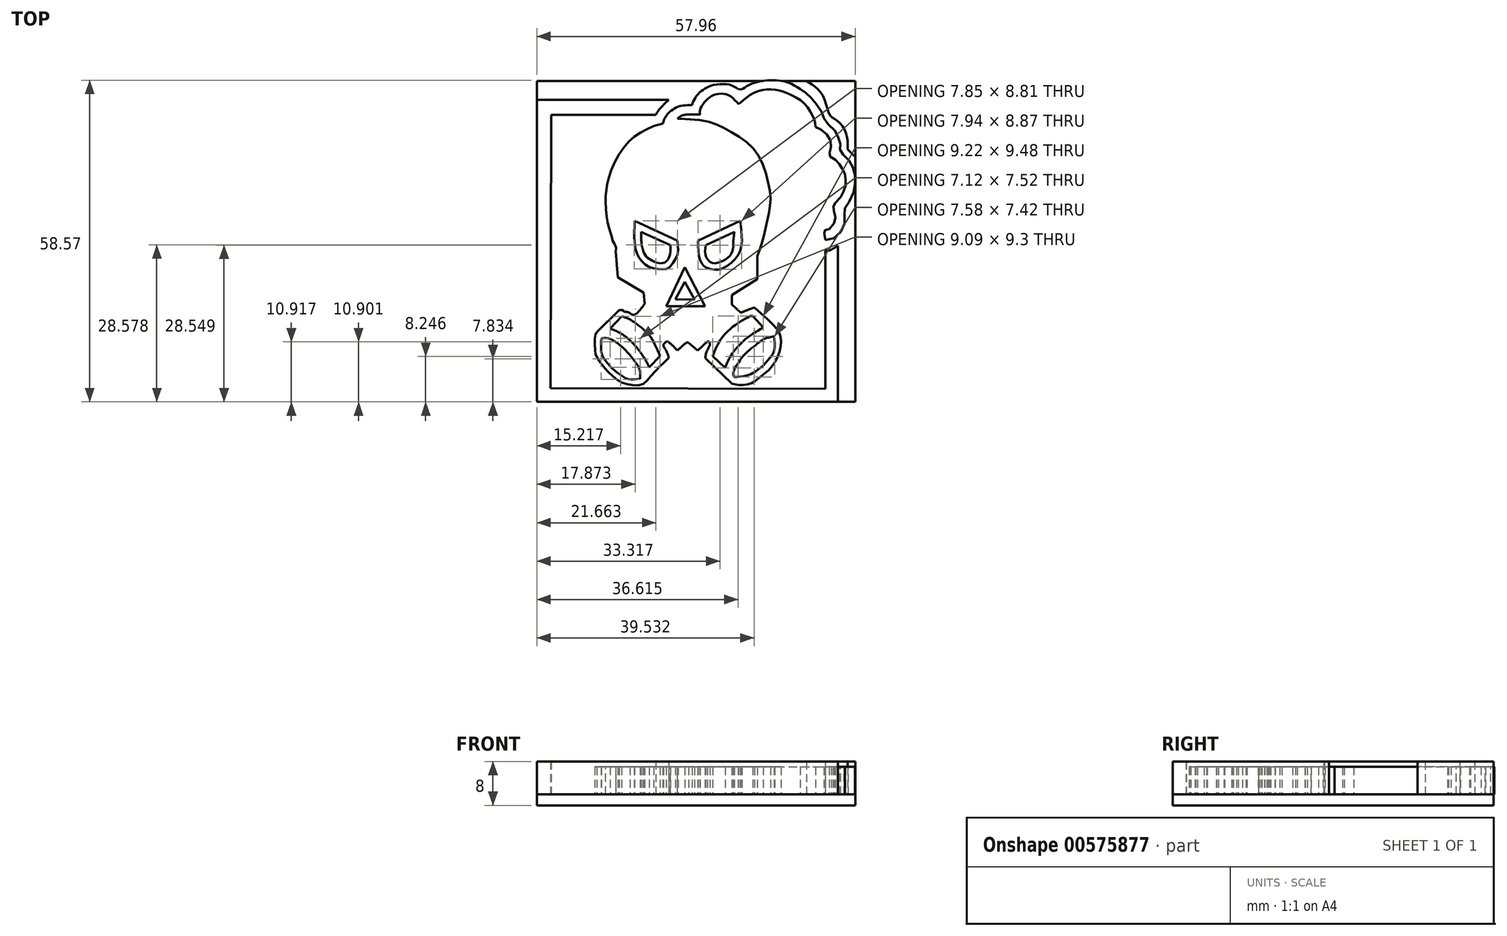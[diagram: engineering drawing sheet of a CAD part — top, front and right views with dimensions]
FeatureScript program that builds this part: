
annotation { "Feature Type Name" : "Feature", "Feature Type Description" : "" }
export const myFeature = defineFeature(function(context is Context, id is Id, definition is map)
    precondition{}
    {
        {
            var Q0;
            Q0=qCreatedBy(makeId("Top.planeOp"),FACE);
            var sketch = newSketch(context, id + "F0", { "sketchPlane" : qUnion([Q0])});
            skFitSpline(sketch, "E0", {"points": [v(4.85, 4.86) * mm, v(54.85, 4.78) * mm], "startDerivative": vector(50, -0.08) * mm, "endDerivative": vector(50, -0.08) * mm});
            skFitSpline(sketch, "E1", {"points": [v(54.85, 4.78) * mm, v(54.85, 29.74) * mm], "startDerivative": vector(0, 24.96) * mm, "endDerivative": vector(0, 24.96) * mm});
            skFitSpline(sketch, "E2", {"points": [v(54.85, 29.74) * mm, v(54.85, 29.98) * mm], "startDerivative": vector(0, 0.24) * mm, "endDerivative": vector(0, 0.24) * mm});
            skFitSpline(sketch, "E3", {"points": [v(54.85, 29.98) * mm, v(55.67, 29.98) * mm, v(56.18, 30.25) * mm, v(56.7, 30.54) * mm, v(57.15, 30.84) * mm, v(57.33, 30.87) * mm], "startDerivative": vector(3.51, -0.37) * mm, "endDerivative": vector(1.39, 0) * mm});
            skFitSpline(sketch, "E4", {"points": [v(57.15, 30.84) * mm, v(57.15, 2.42) * mm], "startDerivative": vector(0, -28.42) * mm, "endDerivative": vector(0, -28.42) * mm});
            skFitSpline(sketch, "E5", {"points": [v(57.15, 2.42) * mm, v(2.35, 2.42) * mm], "startDerivative": vector(-54.8, 0) * mm, "endDerivative": vector(-54.8, 0) * mm});
            skFitSpline(sketch, "E6", {"points": [v(2.35, 2.42) * mm, v(2.35, 57.4) * mm], "startDerivative": vector(0, 54.94) * mm, "endDerivative": vector(0, 54.94) * mm});
            skFitSpline(sketch, "E7", {"points": [v(2.35, 57.4) * mm, v(26.35, 57.4) * mm], "startDerivative": vector(24.68, 0) * mm, "endDerivative": vector(24.68, 0) * mm});
            skFitSpline(sketch, "E8", {"points": [v(26.35, 57.4) * mm, v(23.98, 54.66) * mm, v(23.63, 52.6) * mm], "startDerivative": vector(-5.14, -4.83) * mm, "endDerivative": vector(-0.06, -4.77) * mm});
            skFitSpline(sketch, "E9", {"points": [v(23.63, 52.6) * mm, v(25.28, 53.05) * mm], "startDerivative": vector(1.65, 0.45) * mm, "endDerivative": vector(1.65, 0.45) * mm});
            skFitSpline(sketch, "E10", {"points": [v(25.28, 53.05) * mm, v(25.4, 53.54) * mm, v(25.65, 54.08) * mm, v(25.98, 54.6) * mm, v(26.48, 55.15) * mm, v(27.56, 55.93) * mm, v(28.84, 56.34) * mm, v(30.58, 56.44) * mm], "startDerivative": vector(0.94, 4.7) * mm, "endDerivative": vector(9.33, 0.14) * mm});
            skFitSpline(sketch, "E11", {"points": [v(30.58, 56.44) * mm, v(30.96, 57.4) * mm, v(31.85, 58.59) * mm, v(32.94, 59.45) * mm, v(34.64, 60.13) * mm, v(37.51, 60.13) * mm, v(38.97, 59.36) * mm], "startDerivative": vector(2.28, 7.29) * mm, "endDerivative": vector(8.97, -6.09) * mm});
            skFitSpline(sketch, "E12", {"points": [v(38.97, 59.36) * mm, v(40.18, 59.65) * mm, v(41.42, 60.33) * mm, v(43.29, 60.8) * mm, v(45.6, 60.95) * mm, v(47.88, 60.62) * mm, v(50.28, 59.36) * mm], "startDerivative": vector(14.4, -4.18) * mm, "endDerivative": vector(11.74, -8.26) * mm});
            skFitSpline(sketch, "E13", {"points": [v(50.28, 59.36) * mm, v(51.28, 58.67) * mm, v(52.3, 57.74) * mm, v(53.42, 56.38) * mm, v(54.43, 54.7) * mm, v(54.73, 53.63) * mm, v(56.28, 52.13) * mm, v(56.93, 51.29) * mm, v(57.5, 49.79) * mm, v(57.63, 48.77) * mm, v(57.55, 48) * mm, v(58.55, 47.04) * mm, v(59.65, 45.6) * mm, v(60.17, 44.12) * mm, v(60.27, 42.4) * mm, v(59.9, 40.3) * mm, v(58.72, 38.04) * mm, v(58.3, 37.37) * mm, v(58.43, 35.77) * mm, v(57.88, 33.68) * mm, v(56.25, 32.12) * mm, v(54.38, 31.93) * mm, v(52.6, 32) * mm, v(52, 30.53) * mm, v(56.18, 30.25) * mm], "startDerivative": vector(28.59, -18.45) * mm, "endDerivative": vector(86.4, 9.51) * mm});
            skFitSpline(sketch, "E14", {"points": [v(58.93, 48.37) * mm, v(60.3, 46.96) * mm], "startDerivative": vector(1.38, -1.41) * mm, "endDerivative": vector(1.38, -1.41) * mm});
            skFitSpline(sketch, "E15", {"points": [v(60.3, 46.96) * mm, v(60.3, 60.84) * mm], "startDerivative": vector(0, 13.88) * mm, "endDerivative": vector(0, 13.88) * mm});
            skFitSpline(sketch, "E16", {"points": [v(60.3, 60.84) * mm, v(51.45, 60.84) * mm], "startDerivative": vector(-8.86, 0) * mm, "endDerivative": vector(-8.86, 0) * mm});
            skFitSpline(sketch, "E17", {"points": [v(51.45, 60.84) * mm, v(53, 59.77) * mm, v(54.72, 57.45) * mm, v(55.67, 54.6) * mm, v(56.8, 53.72) * mm, v(58.28, 52.11) * mm, v(58.93, 49.68) * mm, v(58.93, 48.37) * mm], "startDerivative": vector(11.4, -6.9) * mm, "endDerivative": vector(-0.57, -10.61) * mm});
            skFitSpline(sketch, "E18", {"points": [v(16.54, 29.62) * mm, v(16.7, 29.74) * mm], "startDerivative": vector(0.15, 0.12) * mm, "endDerivative": vector(0.15, 0.12) * mm});
            skFitSpline(sketch, "E19", {"points": [v(16.7, 29.74) * mm, v(17.07, 25.04) * mm], "startDerivative": vector(0.37, -4.7) * mm, "endDerivative": vector(0.37, -4.7) * mm});
            skFitSpline(sketch, "E20", {"points": [v(17.07, 25.04) * mm, v(21.8, 22.26) * mm], "startDerivative": vector(4.74, -2.78) * mm, "endDerivative": vector(4.74, -2.78) * mm});
            skFitSpline(sketch, "E21", {"points": [v(21.8, 22.26) * mm, v(21.95, 20.22) * mm], "startDerivative": vector(0.14, -2.03) * mm, "endDerivative": vector(0.14, -2.03) * mm});
            skFitSpline(sketch, "E22", {"points": [v(21.95, 20.22) * mm, v(20.25, 18.31) * mm, v(19.67, 18.28) * mm, v(19.28, 18.51) * mm], "startDerivative": vector(-3.51, -4.76) * mm, "endDerivative": vector(-1.67, 1.18) * mm});
            skFitSpline(sketch, "E23", {"points": [v(19.28, 18.51) * mm, v(18.83, 18.74) * mm, v(18.1, 18.88) * mm, v(18.06, 19.06) * mm, v(17.34, 19.1) * mm], "startDerivative": vector(-1.44, 1.12) * mm, "endDerivative": vector(-3.3, -0.3) * mm});
            skFitSpline(sketch, "E24", {"points": [v(17.34, 19.1) * mm, v(13.24, 15.08) * mm], "startDerivative": vector(-4.1, -4.02) * mm, "endDerivative": vector(-4.1, -4.02) * mm});
            skFitSpline(sketch, "E25", {"points": [v(13.24, 15.08) * mm, v(13, 14.65) * mm, v(12.9, 13.24) * mm, v(12.98, 11.35) * mm, v(13.24, 10.59) * mm, v(13.87, 9.58) * mm, v(14.67, 8.6) * mm, v(15.98, 7.23) * mm, v(17.7, 5.97) * mm, v(19.28, 5.5) * mm, v(21.4, 5.49) * mm, v(22.73, 6.67) * mm, v(24.54, 8.6) * mm, v(26.35, 10.39) * mm], "startDerivative": vector(-6.78, -8.44) * mm, "endDerivative": vector(18.54, 18.04) * mm});
            skFitSpline(sketch, "E26", {"points": [v(26.35, 10.39) * mm, v(26.2, 10.94) * mm, v(25.84, 11.8) * mm, v(25.4, 12.73) * mm, v(25.92, 13.33) * mm], "startDerivative": vector(-0.59, 2.55) * mm, "endDerivative": vector(3.08, 2.22) * mm});
            skFitSpline(sketch, "E27", {"points": [v(25.92, 13.33) * mm, v(26.18, 13.33) * mm, v(27.85, 11.83) * mm], "startDerivative": vector(0.88, 0.26) * mm, "endDerivative": vector(2.68, -2.76) * mm});
            skFitSpline(sketch, "E28", {"points": [v(27.85, 11.83) * mm, v(27.96, 11.75) * mm], "startDerivative": vector(0.12, -0.08) * mm, "endDerivative": vector(0.12, -0.08) * mm});
            skFitSpline(sketch, "E29", {"points": [v(27.96, 11.75) * mm, v(29.62, 13.15) * mm, v(29.98, 13.14) * mm], "startDerivative": vector(2.72, 2.7) * mm, "endDerivative": vector(1.08, -0.33) * mm});
            skFitSpline(sketch, "E30", {"points": [v(29.98, 13.14) * mm, v(31.63, 11.75) * mm], "startDerivative": vector(1.65, -1.4) * mm, "endDerivative": vector(1.65, -1.4) * mm});
            skFitSpline(sketch, "E31", {"points": [v(31.63, 11.75) * mm, v(33.39, 13.41) * mm], "startDerivative": vector(1.76, 1.66) * mm, "endDerivative": vector(1.76, 1.66) * mm});
            skFitSpline(sketch, "E32", {"points": [v(33.39, 13.41) * mm, v(33.78, 13.17) * mm, v(33.79, 12.62) * mm, v(33.5, 12) * mm, v(33.1, 11.04) * mm, v(33.04, 10.3) * mm], "startDerivative": vector(2.94, -1.02) * mm, "endDerivative": vector(0.03, -3.37) * mm});
            skFitSpline(sketch, "E33", {"points": [v(33.04, 10.3) * mm, v(37.84, 5.7) * mm], "startDerivative": vector(4.8, -4.6) * mm, "endDerivative": vector(4.8, -4.6) * mm});
            skFitSpline(sketch, "E34", {"points": [v(37.84, 5.7) * mm, v(39.15, 5.47) * mm, v(41.21, 5.7) * mm, v(42.6, 6.64) * mm, v(44.47, 8.08) * mm, v(46.27, 10.75) * mm, v(46.79, 13.41) * mm, v(46.36, 15.17) * mm, v(41.94, 19.55) * mm], "startDerivative": vector(13.23, -3.15) * mm, "endDerivative": vector(-28.34, 24.51) * mm});
            skFitSpline(sketch, "E35", {"points": [v(41.94, 19.55) * mm, v(41.4, 19.38) * mm, v(40.3, 18.96) * mm, v(39.46, 18.63) * mm], "startDerivative": vector(-1.82, -0.5) * mm, "endDerivative": vector(-2.31, -0.92) * mm});
            skFitSpline(sketch, "E36", {"points": [v(39.46, 18.63) * mm, v(37.84, 20.08) * mm], "startDerivative": vector(-1.62, 1.46) * mm, "endDerivative": vector(-1.62, 1.46) * mm});
            skFitSpline(sketch, "E37", {"points": [v(37.84, 20.08) * mm, v(37.84, 21.85) * mm], "startDerivative": vector(0, 1.77) * mm, "endDerivative": vector(0, 1.77) * mm});
            skFitSpline(sketch, "E38", {"points": [v(37.84, 21.85) * mm, v(42.47, 24.74) * mm], "startDerivative": vector(4.64, 2.9) * mm, "endDerivative": vector(4.64, 2.9) * mm});
            skFitSpline(sketch, "E39", {"points": [v(42.47, 24.74) * mm, v(42.47, 28.94) * mm], "startDerivative": vector(0, 4.2) * mm, "endDerivative": vector(0, 4.2) * mm});
            skFitSpline(sketch, "E40", {"points": [v(42.47, 28.94) * mm, v(43.34, 31.38) * mm, v(44.23, 35.3) * mm, v(44.87, 38.88) * mm, v(44.27, 43.1) * mm, v(41.94, 48.3) * mm, v(37.84, 51.46) * mm, v(33.85, 53.32) * mm, v(27.96, 53.99) * mm], "startDerivative": vector(9.51, 23.54) * mm, "endDerivative": vector(-43.14, 2.06) * mm});
            skFitSpline(sketch, "E41", {"points": [v(27.96, 53.99) * mm, v(28.4, 53.97) * mm], "startDerivative": vector(0.45, -0.02) * mm, "endDerivative": vector(0.45, -0.02) * mm});
            skFitSpline(sketch, "E42", {"points": [v(27.96, 53.99) * mm, v(29.02, 54.6) * mm, v(32.05, 54.69) * mm], "startDerivative": vector(2.29, 1.89) * mm, "endDerivative": vector(5.64, -0.33) * mm});
            skFitSpline(sketch, "E43", {"points": [v(32.05, 54.69) * mm, v(32.05, 55.57) * mm, v(33.04, 57.17) * mm, v(34.77, 58.34) * mm, v(37.17, 58.3) * mm, v(39.02, 56.6) * mm], "startDerivative": vector(-0.96, 6.05) * mm, "endDerivative": vector(7.21, -8.91) * mm});
            skFitSpline(sketch, "E44", {"points": [v(39.02, 56.6) * mm, v(40.03, 57.4) * mm, v(41.5, 58.49) * mm, v(43.51, 59.2) * mm, v(45.5, 59.28) * mm, v(47.22, 58.85) * mm, v(49.66, 57.75) * mm, v(51.6, 56.06) * mm, v(52.9, 53.61) * mm, v(53.07, 52.43) * mm], "startDerivative": vector(10.88, 8.42) * mm, "endDerivative": vector(0.5, -12.4) * mm});
            skFitSpline(sketch, "E45", {"points": [v(53.07, 52.43) * mm, v(54.07, 51.95) * mm, v(55.44, 50.7) * mm, v(55.92, 49.33) * mm, v(55.69, 47.96) * mm, v(55.57, 47.48) * mm, v(55.87, 46.94) * mm, v(56.88, 46.35) * mm, v(57.48, 45.57) * mm, v(57.95, 44.8) * mm, v(58.43, 43.78) * mm, v(58.55, 42.7) * mm, v(58.5, 41.46) * mm, v(58.02, 40.33) * mm, v(57.31, 39.2) * mm, v(56.24, 38.13) * mm, v(56.42, 37.71) * mm, v(56.48, 36.52) * mm, v(56.72, 35.69) * mm, v(56.07, 34.38) * mm, v(55.12, 33.6) * mm, v(54.65, 33.61) * mm, v(54.68, 33.21) * mm, v(54.84, 31.87) * mm], "startDerivative": vector(20.86, -8.3) * mm, "endDerivative": vector(7.9, -24.33) * mm});
            skFitSpline(sketch, "E46", {"points": [v(18.23, 25.9) * mm, v(22.93, 22.86) * mm], "startDerivative": vector(4.7, -3.05) * mm, "endDerivative": vector(4.7, -3.05) * mm});
            skFitSpline(sketch, "E47", {"points": [v(22.93, 22.86) * mm, v(22.93, 19.55) * mm], "startDerivative": vector(0, -3.3) * mm, "endDerivative": vector(0, -3.3) * mm});
            skFitSpline(sketch, "E48", {"points": [v(22.93, 19.55) * mm, v(21.19, 17.92) * mm], "startDerivative": vector(-1.74, -1.64) * mm, "endDerivative": vector(-1.74, -1.64) * mm});
            skFitSpline(sketch, "E49", {"points": [v(21.19, 17.92) * mm, v(22.5, 17.06) * mm, v(23.49, 16.03) * mm, v(24.4, 14.83) * mm, v(24.82, 14.03) * mm, v(25.12, 13.96) * mm, v(25.53, 14.45) * mm, v(25.97, 14.79) * mm, v(26.34, 14.8) * mm, v(26.78, 14.27) * mm, v(27.2, 13.9) * mm, v(27.93, 13.19) * mm], "startDerivative": vector(10.98, -6.4) * mm, "endDerivative": vector(7.58, -7.87) * mm});
            skFitSpline(sketch, "E50", {"points": [v(27.93, 13.19) * mm, v(29.79, 14.92) * mm], "startDerivative": vector(1.85, 1.73) * mm, "endDerivative": vector(1.85, 1.73) * mm});
            skFitSpline(sketch, "E51", {"points": [v(29.79, 14.92) * mm, v(31.6, 13.19) * mm], "startDerivative": vector(1.82, -1.73) * mm, "endDerivative": vector(1.82, -1.73) * mm});
            skFitSpline(sketch, "E52", {"points": [v(31.6, 13.19) * mm, v(33.44, 14.92) * mm], "startDerivative": vector(1.83, 1.73) * mm, "endDerivative": vector(1.83, 1.73) * mm});
            skFitSpline(sketch, "E53", {"points": [v(33.44, 14.92) * mm, v(34.61, 13.96) * mm], "startDerivative": vector(1.17, -0.95) * mm, "endDerivative": vector(1.17, -0.95) * mm});
            skFitSpline(sketch, "E54", {"points": [v(34.61, 13.96) * mm, v(34.61, 14.41) * mm, v(35.43, 15.54) * mm, v(36.28, 16.46) * mm, v(38.2, 17.92) * mm], "startDerivative": vector(-0.63, 2.75) * mm, "endDerivative": vector(6.33, 4.47) * mm});
            skFitSpline(sketch, "E55", {"points": [v(38.2, 17.92) * mm, v(36.53, 19.55) * mm], "startDerivative": vector(-1.68, 1.64) * mm, "endDerivative": vector(-1.68, 1.64) * mm});
            skFitSpline(sketch, "E56", {"points": [v(36.53, 19.55) * mm, v(36.53, 22.86) * mm], "startDerivative": vector(0, 3.3) * mm, "endDerivative": vector(0, 3.3) * mm});
            skFitSpline(sketch, "E57", {"points": [v(36.53, 22.86) * mm, v(41.34, 25.9) * mm], "startDerivative": vector(4.81, 3.05) * mm, "endDerivative": vector(4.81, 3.05) * mm});
            skFitSpline(sketch, "E58", {"points": [v(41.34, 25.9) * mm, v(41.34, 29.15) * mm, v(42, 31.3) * mm, v(42.47, 33.75) * mm, v(43.2, 36.6) * mm, v(43.18, 41.86) * mm, v(41.34, 46.73) * mm, v(37.85, 50.02) * mm, v(35.13, 51.62) * mm], "startDerivative": vector(-2.15, 28.98) * mm, "endDerivative": vector(-23.66, 9.66) * mm});
            skFitSpline(sketch, "E59", {"points": [v(35.13, 51.62) * mm, v(34.47, 51.85) * mm, v(32.8, 52.45) * mm, v(31.13, 52.77) * mm, v(29.24, 52.9) * mm, v(27.39, 52.57) * mm, v(25.25, 51.88) * mm, v(23.7, 51.34) * mm, v(21.93, 50.33) * mm, v(20.35, 49.26) * mm, v(18.93, 47.6) * mm, v(18.13, 46.15) * mm, v(17.28, 44.31) * mm, v(16.51, 41.94) * mm, v(16.21, 40.6) * mm, v(16.22, 36.88) * mm, v(16.7, 35.08) * mm, v(17.17, 33.36) * mm, v(17.64, 31.54) * mm, v(17.9, 29.94) * mm, v(18.15, 26.66) * mm, v(18.23, 25.9) * mm], "startDerivative": vector(-19.6, 6.77) * mm, "endDerivative": vector(2.06, -18.95) * mm});
            skFitSpline(sketch, "E60", {"points": [v(27.58, 21.04) * mm, v(29.3, 24.23) * mm], "startDerivative": vector(1.7, 3.18) * mm, "endDerivative": vector(1.7, 3.18) * mm});
            skFitSpline(sketch, "E61", {"points": [v(29.3, 24.23) * mm, v(31.07, 20.98) * mm], "startDerivative": vector(1.77, -3.24) * mm, "endDerivative": vector(1.77, -3.24) * mm});
            skFitSpline(sketch, "E62", {"points": [v(31.07, 20.98) * mm, v(27.58, 21.04) * mm], "startDerivative": vector(-3.48, 0.06) * mm, "endDerivative": vector(-3.48, 0.06) * mm});
            skFitSpline(sketch, "E63", {"points": [v(25.88, 19.8) * mm, v(32.94, 19.82) * mm], "startDerivative": vector(7.06, 0.02) * mm, "endDerivative": vector(7.06, 0.02) * mm});
            skFitSpline(sketch, "E64", {"points": [v(32.94, 19.82) * mm, v(29.3, 26.88) * mm], "startDerivative": vector(-3.65, 7.05) * mm, "endDerivative": vector(-3.65, 7.05) * mm});
            skFitSpline(sketch, "E65", {"points": [v(29.3, 26.88) * mm, v(25.88, 19.8) * mm], "startDerivative": vector(-3.41, -7.07) * mm, "endDerivative": vector(-3.41, -7.07) * mm});
            skFitSpline(sketch, "E66", {"points": [v(26.64, 30.89) * mm, v(21.31, 33.31) * mm], "startDerivative": vector(-5.33, 2.43) * mm, "endDerivative": vector(-5.33, 2.43) * mm});
            skFitSpline(sketch, "E67", {"points": [v(33.07, 30.89) * mm, v(33.07, 29.07) * mm, v(34.17, 27.7) * mm, v(35.97, 27.95) * mm, v(37.23, 28.75) * mm, v(37.99, 29.92) * mm, v(38.11, 31.29) * mm, v(38.28, 33.31) * mm], "startDerivative": vector(-1.6, -12.2) * mm, "endDerivative": vector(1.39, 13.4) * mm});
            skFitSpline(sketch, "E68", {"points": [v(38.28, 33.31) * mm, v(33.07, 30.89) * mm], "startDerivative": vector(-5.2, -2.43) * mm, "endDerivative": vector(-5.2, -2.43) * mm});
            skFitSpline(sketch, "E69", {"points": [v(27.91, 31.73) * mm, v(27.88, 29.07) * mm, v(26.64, 27.06) * mm, v(26.03, 26.64) * mm, v(23.88, 26.65) * mm, v(21.7, 27.7) * mm, v(20.4, 29.92) * mm, v(20.1, 32) * mm, v(20.13, 35.38) * mm], "startDerivative": vector(2.63, -19.72) * mm, "endDerivative": vector(0.59, 23.4) * mm});
            skFitSpline(sketch, "E70", {"points": [v(20.13, 35.38) * mm, v(27.91, 31.73) * mm], "startDerivative": vector(7.79, -3.64) * mm, "endDerivative": vector(7.79, -3.64) * mm});
            skFitSpline(sketch, "E71", {"points": [v(39.39, 35.38) * mm, v(39.64, 32.59) * mm, v(39.35, 29.92) * mm, v(37.76, 27.7) * mm, v(35.97, 26.61) * mm, v(35.28, 26.5) * mm, v(33.4, 26.7) * mm, v(32.3, 27.7) * mm, v(31.83, 29.07) * mm, v(31.7, 31.73) * mm], "startDerivative": vector(2.48, -21) * mm, "endDerivative": vector(-0.18, 22.42) * mm});
            skFitSpline(sketch, "E72", {"points": [v(31.7, 31.73) * mm, v(39.39, 35.38) * mm], "startDerivative": vector(7.69, 3.64) * mm, "endDerivative": vector(7.69, 3.64) * mm});
            skFitSpline(sketch, "E73", {"points": [v(15.68, 15.73) * mm, v(17.77, 17.96) * mm], "startDerivative": vector(2.1, 2.23) * mm, "endDerivative": vector(2.1, 2.23) * mm});
            skFitSpline(sketch, "E74", {"points": [v(17.77, 17.96) * mm, v(18.64, 17.68) * mm, v(19.86, 17.03) * mm, v(21.02, 16.18) * mm, v(22.45, 14.96) * mm, v(23.63, 13.2) * mm, v(24.77, 10.72) * mm], "startDerivative": vector(6.78, -1.82) * mm, "endDerivative": vector(5.28, -12.24) * mm});
            skFitSpline(sketch, "E75", {"points": [v(24.77, 10.72) * mm, v(22.8, 8.66) * mm], "startDerivative": vector(-1.97, -2.06) * mm, "endDerivative": vector(-1.97, -2.06) * mm});
            skFitSpline(sketch, "E76", {"points": [v(22.8, 8.66) * mm, v(22.3, 9.7) * mm, v(20.39, 12.45) * mm], "startDerivative": vector(-0.9, 2.26) * mm, "endDerivative": vector(-2.04, 2.2) * mm});
            skFitSpline(sketch, "E77", {"points": [v(20.39, 12.45) * mm, v(19.43, 13.45) * mm, v(18.3, 14.4) * mm, v(16.93, 15.2) * mm, v(15.68, 15.73) * mm], "startDerivative": vector(-3.83, 4.12) * mm, "endDerivative": vector(-5.14, 1.99) * mm});
            skFitSpline(sketch, "E78", {"points": [v(34.36, 10.72) * mm, v(36.6, 8.55) * mm], "startDerivative": vector(2.25, -2.16) * mm, "endDerivative": vector(2.25, -2.16) * mm});
            skFitSpline(sketch, "E79", {"points": [v(36.6, 8.55) * mm, v(37.1, 9.75) * mm, v(37.87, 11.07) * mm, v(40.15, 13.66) * mm, v(43.57, 15.94) * mm], "startDerivative": vector(2.5, 6.71) * mm, "endDerivative": vector(11.06, 6.4) * mm});
            skFitSpline(sketch, "E80", {"points": [v(43.57, 15.94) * mm, v(41.65, 18.03) * mm], "startDerivative": vector(-1.92, 2.09) * mm, "endDerivative": vector(-1.92, 2.09) * mm});
            skFitSpline(sketch, "E81", {"points": [v(41.65, 18.03) * mm, v(41.27, 18.03) * mm, v(40.25, 17.48) * mm, v(38.13, 16.16) * mm, v(36.18, 14.24) * mm, v(35.09, 12.45) * mm, v(34.36, 10.72) * mm], "startDerivative": vector(-4.37, 0.68) * mm, "endDerivative": vector(-3.85, -9.85) * mm});
            skFitSpline(sketch, "E82", {"points": [v(45.51, 14.35) * mm, v(45.58, 11.85) * mm, v(44.47, 10.03) * mm, v(43.02, 8.55) * mm, v(42.06, 7.88) * mm, v(41.4, 7.51) * mm, v(40.3, 7.12) * mm, v(38.24, 6.92) * mm], "startDerivative": vector(2.16, -14.74) * mm, "endDerivative": vector(-12.38, 0) * mm});
            skFitSpline(sketch, "E83", {"points": [v(38.24, 6.92) * mm, v(38.24, 8.08) * mm], "startDerivative": vector(-0.6, 1.01) * mm, "endDerivative": vector(0.62, 1.06) * mm});
            skFitSpline(sketch, "E84", {"points": [v(38.24, 8.08) * mm, v(38.43, 8.54) * mm, v(39.19, 9.7) * mm, v(39.6, 10.35) * mm, v(40.83, 11.68) * mm, v(42.15, 12.7) * mm, v(43.74, 13.88) * mm, v(45.51, 14.35) * mm], "startDerivative": vector(1.35, 4.6) * mm, "endDerivative": vector(11, 4.12) * mm});
            skFitSpline(sketch, "E85", {"points": [v(21.12, 6.6) * mm, v(18.94, 6.53) * mm, v(17.65, 7.24) * mm, v(16.24, 8.3) * mm, v(14.97, 9.7) * mm, v(14.1, 11.37) * mm, v(14.12, 13.98) * mm], "startDerivative": vector(-13.43, -1.84) * mm, "endDerivative": vector(1.48, 14.42) * mm});
            skFitSpline(sketch, "E86", {"points": [v(14.12, 13.98) * mm, v(15.34, 13.98) * mm, v(16.5, 13.41) * mm, v(17.88, 12.36) * mm, v(19.43, 10.72) * mm, v(20.86, 8.7) * mm, v(21.12, 7.84) * mm, v(21.12, 6.6) * mm], "startDerivative": vector(9.8, 1) * mm, "endDerivative": vector(-0.38, -10.36) * mm});
            skFitSpline(sketch, "E87", {"points": [v(23.98, 54.66) * mm, v(4.92, 54.66) * mm], "startDerivative": vector(-19.06, 0) * mm, "endDerivative": vector(-19.06, 0) * mm});
            skFitSpline(sketch, "E88", {"points": [v(4.92, 54.66) * mm, v(4.85, 4.86) * mm], "startDerivative": vector(-0.07, -49.8) * mm, "endDerivative": vector(-0.07, -49.8) * mm});
            skFitSpline(sketch, "E89", {"points": [v(16.7, 29.74) * mm, v(16.7, 30.67) * mm, v(16.21, 31.55) * mm, v(15.96, 32.46) * mm, v(15.56, 33.82) * mm, v(15.09, 35.79) * mm, v(14.86, 39.14) * mm, v(14.98, 41) * mm, v(15.7, 44.07) * mm, v(17.9, 48.36) * mm, v(20.56, 51.04) * mm, v(23.63, 52.6) * mm], "startDerivative": vector(2.36, 16.27) * mm, "endDerivative": vector(28.37, 12.21) * mm});
            skFitSpline(sketch, "E90", {"points": [v(26.64, 30.89) * mm, v(26.64, 29.4) * mm, v(26.44, 28.82) * mm, v(26.17, 28.28) * mm, v(25.71, 27.83) * mm, v(25.1, 27.63) * mm, v(24.27, 27.71) * mm, v(23.5, 28) * mm, v(22.75, 28.44) * mm, v(22.23, 28.89) * mm, v(21.84, 29.52) * mm, v(21.64, 30.13) * mm], "startDerivative": vector(0.77, -13.17) * mm, "endDerivative": vector(-1.87, 7.33) * mm});
            skFitSpline(sketch, "E91", {"points": [v(21.64, 30.13) * mm, v(21.5, 30.62) * mm, v(21.4, 31.22) * mm, v(21.31, 33.31) * mm], "startDerivative": vector(-0.62, 2.06) * mm, "endDerivative": vector(-0.1, 4.92) * mm});
            skSolve(sketch);
        }
        {
            var Q0;
            Q0=makeQuery(id+"F0.imprint","IMPRINT",FACE,{"disambiguationData":[TD([[makeQuery(id+"F0.imprint","IMPRINT",EDGE,{"derivedFrom":sQuery(id+"F0.wireOp",EDGE,"E14")}),1.0]])]});
            var Q1;
            Q1=makeQuery(id+"F0.imprint","IMPRINT",FACE,{"disambiguationData":[TD([[makeQuery(id+"F0.imprint","IMPRINT",EDGE,{"derivedFrom":sQuery(id+"F0.wireOp",EDGE,"E0")}),-1.0]])]});
            var Q2;
            Q2=makeQuery(id+"F0.imprint","IMPRINT",FACE,{"disambiguationData":[TD([[makeQuery(id+"F0.imprint","IMPRINT",EDGE,{"derivedFrom":sQuery(id+"F0.wireOp",EDGE,"E46")}),1.0]])]});
            var Q3;
            Q3=makeQuery(id+"F0.imprint","IMPRINT",FACE,{"disambiguationData":[TD([[makeQuery(id+"F0.imprint","IMPRINT",EDGE,{"derivedFrom":sQuery(id+"F0.wireOp",EDGE,"814c325e-e478-47b2-9197-f5db7bca019a")}),1.0]])]});
            var Q4;
            Q4=makeQuery(id+"F0.imprint","IMPRINT",FACE,{"disambiguationData":[TD([[makeQuery(id+"F0.imprint","IMPRINT",EDGE,{"derivedFrom":sQuery(id+"F0.wireOp",EDGE,"E67")}),1.0]])]});
            var Q5;
            Q5=makeQuery(id+"F0.imprint","IMPRINT",FACE,{"disambiguationData":[TD([[makeQuery(id+"F0.imprint","IMPRINT",EDGE,{"derivedFrom":sQuery(id+"F0.wireOp",EDGE,"E9")}),-1.0]])]});
            var Q6;
            Q6=makeQuery(id+"F0.imprint","IMPRINT",FACE,{"disambiguationData":[TD([[makeQuery(id+"F0.imprint","IMPRINT",EDGE,{"derivedFrom":sQuery(id+"F0.wireOp",EDGE,"E66")}),1.0]])]});
            var Q7;
            Q7=makeQuery(id+"F0.imprint","IMPRINT",FACE,{"disambiguationData":[TD([[makeQuery(id+"F0.imprint","IMPRINT",EDGE,{"derivedFrom":sQuery(id+"F0.wireOp",EDGE,"E60")}),-1.0]])]});
            extrude(context, id + "F1", {"entities" : qUnion([Q0, Q1, Q2, Q3, Q4, Q5, Q6, Q7]), "depth" : 5 * mm, "offsetDistance" : 25 * mm});
        }
        {
            var Q0;
            {var subQ0=sQuery(id+"F0.wireOp",EDGE,"6d4c8553-d6a6-41d1-a501-11ceb255abb1");Q0=makeQuery(id+"F0.imprint","IMPRINT",FACE,{"disambiguationData":[TD([[makeQuery(id+"F0.imprint","IMPRINT",EDGE,{"derivedFrom":subQ0}),1.0]])]});}
            var Q1;
            {var subQ0=sQuery(id+"F0.wireOp",EDGE,"104c1b62-f294-46fb-9bf6-65a114937dfa");Q1=makeQuery(id+"F0.imprint","IMPRINT",FACE,{"disambiguationData":[TD([[makeQuery(id+"F0.imprint","IMPRINT",EDGE,{"derivedFrom":subQ0}),1.0]])]});}
            var Q2;
            {var subQ0=sQuery(id+"F0.wireOp",EDGE,"1577cb91-bc54-4e5b-8a2f-d5ec2b630157");Q2=makeQuery(id+"F0.imprint","IMPRINT",FACE,{"disambiguationData":[TD([[makeQuery(id+"F0.imprint","IMPRINT",EDGE,{"derivedFrom":subQ0}),1.0]])]});}
            var Q3;
            {var subQ0=sQuery(id+"F0.wireOp",EDGE,"ce8b6f23-e2b7-4828-a9f3-254046c45328");Q3=makeQuery(id+"F0.imprint","IMPRINT",FACE,{"disambiguationData":[TD([[makeQuery(id+"F0.imprint","IMPRINT",EDGE,{"derivedFrom":subQ0}),1.0]])]});}
            var Q4;
            Q4=makeQuery(id+"F1.opExtrude","CAP_FACE",FACE,{"disambiguationData":[OSD([sQuery(id+"F0.wireOp",EDGE,"E0"),sQuery(id+"F0.wireOp",EDGE,"E1"),sQuery(id+"F0.wireOp",EDGE,"E2"),sQuery(id+"F0.wireOp",EDGE,"E3"),sQuery(id+"F0.wireOp",EDGE,"E4"),sQuery(id+"F0.wireOp",EDGE,"E5"),sQuery(id+"F0.wireOp",EDGE,"E6"),sQuery(id+"F0.wireOp",EDGE,"E7"),sQuery(id+"F0.wireOp",EDGE,"E8"),sQuery(id+"F0.wireOp",EDGE,"E87"),sQuery(id+"F0.wireOp",EDGE,"E88")])],"isStart":false});
            var Q5;
            Q5=makeQuery(id+"F1.opExtrude","CAP_FACE",FACE,{"disambiguationData":[OSD([sQuery(id+"F0.wireOp",EDGE,"E14"),sQuery(id+"F0.wireOp",EDGE,"E15"),sQuery(id+"F0.wireOp",EDGE,"E16"),sQuery(id+"F0.wireOp",EDGE,"E17")])],"isStart":false});
            extrude(context, id + "F2", {"entities" : qUnion([Q0, Q1, Q2, Q3, Q4, Q5]), "operationType" : NewBodyOperationType.ADD, "depth" : 1 * mm, "offsetDistance" : 25 * mm});
        }
        {
            var Q0;
            Q0=makeQuery(id+"F1.opExtrude","CAP_FACE",FACE,{"disambiguationData":[OSD([sQuery(id+"F0.wireOp",EDGE,"E14"),sQuery(id+"F0.wireOp",EDGE,"E15"),sQuery(id+"F0.wireOp",EDGE,"E16"),sQuery(id+"F0.wireOp",EDGE,"E17")])],"isStart":true});
            var sketch = newSketch(context, id + "F3", { "sketchPlane" : qUnion([Q0])});
            skLineSegment(sketch, "E92", {"start": v(60.3, -60.84) * mm, "end": v(2.38, -60.84) * mm});
            skLineSegment(sketch, "E93", {"start": v(2.38, -60.84) * mm, "end": v(2.38, -2.42) * mm});
            skLineSegment(sketch, "E94", {"start": v(60.3, -60.84) * mm, "end": v(60.3, -2.4) * mm});
            skLineSegment(sketch, "E95", {"start": v(60.3, -2.4) * mm, "end": v(2.38, -2.42) * mm});
            skSolve(sketch);
        }
        {
            var Q0;
            Q0 = qSketchRegion(id + "F3", true);
            extrude(context, id + "F4", {"entities" : qUnion([Q0]), "depth" : 2 * mm, "offsetDistance" : 25 * mm});
        }
    });
